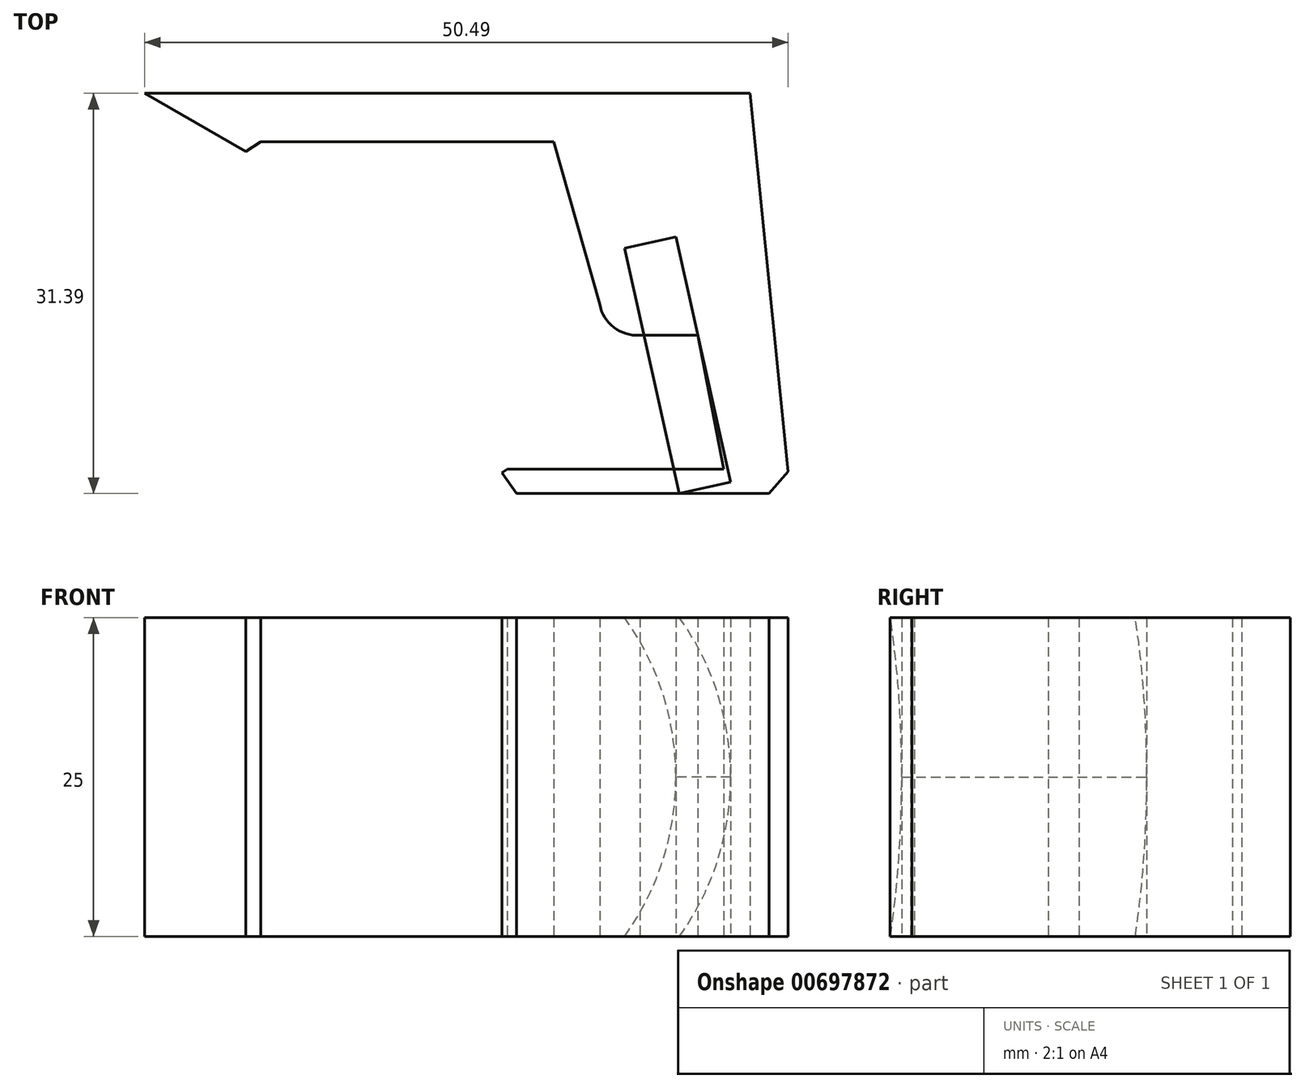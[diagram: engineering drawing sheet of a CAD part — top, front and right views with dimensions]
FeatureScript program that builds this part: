
annotation { "Feature Type Name" : "Feature", "Feature Type Description" : "" }
export const myFeature = defineFeature(function(context is Context, id is Id, definition is map)
    precondition{}
    {
        {
            var Q0;
            Q0=qCreatedBy(makeId("Top.planeOp"),FACE);
            var sketch = newSketch(context, id + "F0", { "sketchPlane" : qUnion([Q0])});
            skLineSegment(sketch, "E0", {"start": v(0, 0) * mm, "end": v(17, 0) * mm});
            skLineSegment(sketch, "E1", {"start": v(0, 0) * mm, "end": v(-0.4, -0.29) * mm});
            skLineSegment(sketch, "E2.4", {"start": v(19.08, 29.47) * mm, "end": v(22.05, -0.2) * mm});
            skLineSegment(sketch, "E3", {"start": v(-0.4, -0.29) * mm, "end": v(0.74, -1.92) * mm});
            skLineSegment(sketch, "E4", {"start": v(0.74, -1.92) * mm, "end": v(20.57, -1.92) * mm});
            skPoint(sketch, "E5.visualSharp", {"position": v(19.38, 26.47) * mm});
            skLineSegment(sketch, "E6", {"start": v(20.57, -1.92) * mm, "end": v(22.05, -0.2) * mm});
            skLineSegment(sketch, "E7", {"start": v(10.43, 10.5) * mm, "end": v(14.96, 10.5) * mm});
            skPoint(sketch, "E8.orphan", {"position": v(8.5, 25.04) * mm});
            skLineSegment(sketch, "E9.0", {"start": v(-28.44, 29.47) * mm, "end": v(19.08, 29.47) * mm});
            skArc(sketch, "E10", {"start": v(7.27, 12.91) * mm, "mid": v(8.4, 11.1) * mm, "end": v(10.43, 10.5) * mm});
            skLineSegment(sketch, "E11", {"start": v(17, 0) * mm, "end": v(14.96, 10.5) * mm});
            skLineSegment(sketch, "E12", {"start": v(7.27, 12.91) * mm, "end": v(3.67, 25.66) * mm});
            skLineSegment(sketch, "E13", {"start": v(3.67, 25.66) * mm, "end": v(-16.32, 25.66) * mm});
            skPoint(sketch, "E13.startSnap0", {"position": v(-16.32, 25.66) * mm});
            skLineSegment(sketch, "E14", {"start": v(-16.32, 25.66) * mm, "end": v(-19.32, 25.66) * mm});
            skLineSegment(sketch, "E15", {"start": v(-19.32, 25.66) * mm, "end": v(-20.5, 24.93) * mm});
            skLineSegment(sketch, "E16", {"start": v(-20.5, 24.93) * mm, "end": v(-28.44, 29.47) * mm});
            skSolve(sketch);
        }
        {
            var Q0;
            Q0=makeQuery(id+"F0.imprint","IMPRINT",FACE,{"disambiguationData":[TD([[makeQuery(id+"F0.imprint","IMPRINT",EDGE,{"derivedFrom":sQuery(id+"F0.wireOp",EDGE,"E0")}),-1.0]])]});
            extrude(context, id + "F1", {"entities" : qUnion([Q0]), "depth" : 25 * mm, "offsetDistance" : 25 * mm});
        }
        {
            var Q0;
            Q0=makeQuery(id+"F1.opExtrude","SWEPT_EDGE",EDGE,{"disambiguationData":[OSD([sQuery(id+"F0.wireOp",EDGE,"E7"),sQuery(id+"F0.wireOp",EDGE,"E11")])]});
            cPlane(context, id + "F2", {"entities" : qUnion([Q0]), "cplaneType" : CPlaneType.LINE_ANGLE, "offset" : 25 * mm, "angle" : 102.6 * degree, "oppositeDirection" : true, "width" : 150 * mm, "height" : 150 * mm});
        }
        {
            var Q0;
            Q0=qCreatedBy(id+"F2.planeOp",FACE);
            var sketch = newSketch(context, id + "F3", { "sketchPlane" : qUnion([Q0])});
            skLineSegment(sketch, "E17", {"start": v(16.9, 25) * mm, "end": v(16.9, 0) * mm});
            skArc(sketch, "E18", {"start": v(12.77, 0) * mm, "mid": v(16.9, 12.5) * mm, "end": v(12.77, 25) * mm});
            skLineSegment(sketch, "E19", {"start": v(16.9, 25) * mm, "end": v(12.77, 25) * mm});
            skLineSegment(sketch, "E20", {"start": v(16.9, 0) * mm, "end": v(12.77, 0) * mm});
            skPoint(sketch, "E21.start.orphan", {"position": v(16.9, 12.5) * mm});
            skSolve(sketch);
        }
        {
            var Q0;
            Q0 = qSketchRegion(id + "F3", true);
            extrude(context, id + "F4", {"entities" : qUnion([Q0]), "depth" : 11.8 * mm, "offsetDistance" : 25 * mm, "hasSecondDirection" : true, "secondDirectionOppositeDirection" : true, "secondDirectionDepth" : 7.9 * mm});
        }
    });
